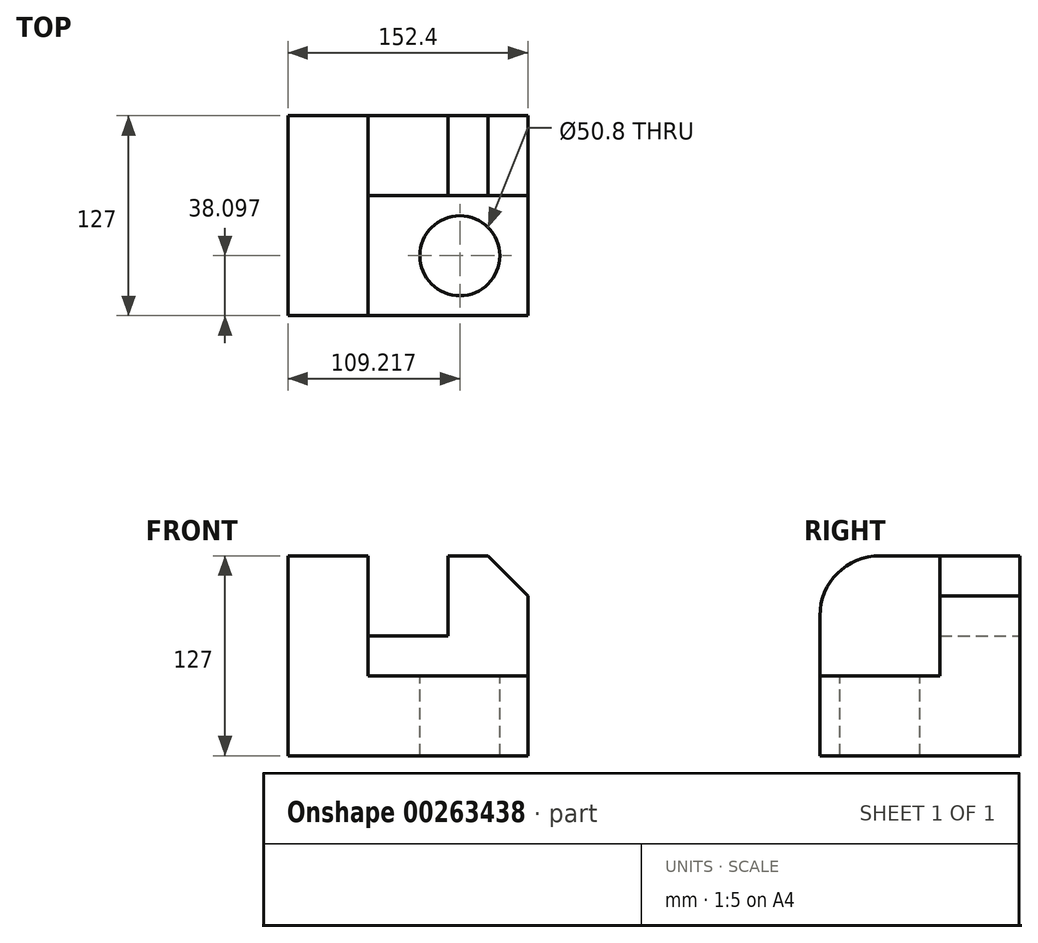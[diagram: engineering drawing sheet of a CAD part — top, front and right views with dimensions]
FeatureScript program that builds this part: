
annotation { "Feature Type Name" : "Feature", "Feature Type Description" : "" }
export const myFeature = defineFeature(function(context is Context, id is Id, definition is map)
    precondition{}
    {
        {
            var Q0;
            Q0=qCreatedBy(makeId("Top.planeOp"),FACE);
            var sketch = newSketch(context, id + "F0", { "sketchPlane" : qUnion([Q0])});
            skLineSegment(sketch, "E0.bottom", {"start": v(-56.85, 59.82) * mm, "end": v(95.55, 59.82) * mm});
            skLineSegment(sketch, "E0.top", {"start": v(-56.85, -67.18) * mm, "end": v(95.55, -67.18) * mm});
            skLineSegment(sketch, "E0.left", {"start": v(-56.85, 59.82) * mm, "end": v(-56.85, -67.18) * mm});
            skLineSegment(sketch, "E0.right", {"start": v(95.55, 59.82) * mm, "end": v(95.55, -67.18) * mm});
            skSolve(sketch);
        }
        {
            var Q0;
            Q0=makeQuery(id+"F0.imprint","IMPRINT",FACE,{"disambiguationData":[TD([[makeQuery(id+"F0.imprint","IMPRINT",EDGE,{"derivedFrom":sQuery(id+"F0.wireOp",EDGE,"E0.bottom")}),-1.0]])]});
            extrude(context, id + "F1", {"entities" : qUnion([Q0]), "depth" : 127 * mm});
        }
        {
            var Q0;
            Q0=makeQuery(id+"F1.opExtrude","CAP_FACE",FACE,{"disambiguationData":[OSD([sQuery(id+"F0.wireOp",EDGE,"E0.bottom"),sQuery(id+"F0.wireOp",EDGE,"E0.top"),sQuery(id+"F0.wireOp",EDGE,"E0.left"),sQuery(id+"F0.wireOp",EDGE,"E0.right")])],"isStart":false});
            var sketch = newSketch(context, id + "F2", { "sketchPlane" : qUnion([Q0])});
            skLineSegment(sketch, "E1", {"start": v(-6.05, -67.18) * mm, "end": v(95.55, -67.18) * mm});
            skLineSegment(sketch, "E2", {"start": v(95.55, -67.18) * mm, "end": v(95.55, 9.02) * mm});
            skLineSegment(sketch, "E3", {"start": v(-6.05, -67.18) * mm, "end": v(-6.05, 9.02) * mm});
            skLineSegment(sketch, "E4", {"start": v(-6.05, 9.02) * mm, "end": v(95.55, 9.02) * mm});
            skSolve(sketch);
        }
        {
            var Q0;
            Q0=makeQuery(id+"F2.imprint","IMPRINT",FACE,{"disambiguationData":[TD([[makeQuery(id+"F2.imprint","IMPRINT",EDGE,{"derivedFrom":sQuery(id+"F2.wireOp",EDGE,"E1")}),1.0]])]});
            extrude(context, id + "F3", {"entities" : qUnion([Q0]), "operationType" : NewBodyOperationType.REMOVE, "oppositeDirection" : true, "depth" : 76.2 * mm});
        }
        {
            var Q0;
            Q0=makeQuery(id+"F1.opExtrude","CAP_EDGE",EDGE,{"disambiguationData":[OSD([sQuery(id+"F0.wireOp",EDGE,"E0.top")])],"isStart":false});
            fillet(context, id + "F4", {"entities" : qUnion([Q0]), "radius" : 38.1 * mm, "tangentPropagation" : true, "allowEdgeOverflow" : false});
        }
        {
            var Q0;
            Q0=makeQuery(id+"F1.opExtrude","CAP_EDGE",EDGE,{"disambiguationData":[OSD([sQuery(id+"F0.wireOp",EDGE,"E0.right")])],"isStart":false});
            chamfer(context, id + "F5", {"entities" : qUnion([Q0]), "width" : 25.4 * mm, "tangentPropagation" : true});
        }
        {
            var Q0;
            Q0=makeQuery(id+"F1.opExtrude","CAP_FACE",FACE,{"disambiguationData":[OSD([sQuery(id+"F0.wireOp",EDGE,"E0.bottom"),sQuery(id+"F0.wireOp",EDGE,"E0.top"),sQuery(id+"F0.wireOp",EDGE,"E0.left"),sQuery(id+"F0.wireOp",EDGE,"E0.right")])],"isStart":false});
            var sketch = newSketch(context, id + "F6", { "sketchPlane" : qUnion([Q0])});
            skLineSegment(sketch, "E5", {"start": v(-6.05, 9.02) * mm, "end": v(-6.05, 59.82) * mm});
            skLineSegment(sketch, "E6", {"start": v(-6.05, 59.82) * mm, "end": v(44.75, 59.82) * mm});
            skLineSegment(sketch, "E7", {"start": v(44.75, 59.82) * mm, "end": v(44.75, 9.02) * mm});
            skLineSegment(sketch, "E8", {"start": v(44.75, 9.02) * mm, "end": v(-6.05, 9.02) * mm});
            skSolve(sketch);
        }
        {
            var Q0;
            Q0 = qSketchRegion(id + "F6", true);
            extrude(context, id + "F7", {"entities" : qUnion([Q0]), "operationType" : NewBodyOperationType.REMOVE, "oppositeDirection" : true, "depth" : 50.8 * mm});
        }
        {
            var Q0;
            Q0=makeQuery(id+"F3.boolean.opBoolean","COPY",FACE,{"derivedFrom":makeQuery(id+"F3.opExtrude","CAP_FACE",FACE,{"disambiguationData":[OSD([sQuery(id+"F2.wireOp",EDGE,"E1"),sQuery(id+"F2.wireOp",EDGE,"E2"),sQuery(id+"F2.wireOp",EDGE,"E3"),sQuery(id+"F2.wireOp",EDGE,"E4")])],"isStart":false})});
            var sketch = newSketch(context, id + "F8", { "sketchPlane" : qUnion([Q0])});
            skCircle(sketch, "E9", {"center": v(52.37, -29.08) * mm, "radius": 25.4 * mm});
            skSolve(sketch);
        }
        {
            var Q0;
            Q0=makeQuery(id+"F8.imprint","IMPRINT",FACE,{"disambiguationData":[TD([[makeQuery(id+"F8.imprint","IMPRINT",EDGE,{"derivedFrom":sQuery(id+"F8.wireOp",EDGE,"E9")}),1.0]])]});
            extrude(context, id + "F9", {"entities" : qUnion([Q0]), "operationType" : NewBodyOperationType.REMOVE, "endBound" : BoundingType.THROUGH_ALL, "oppositeDirection" : true, "depth" : 25.4 * mm});
        }
    });
